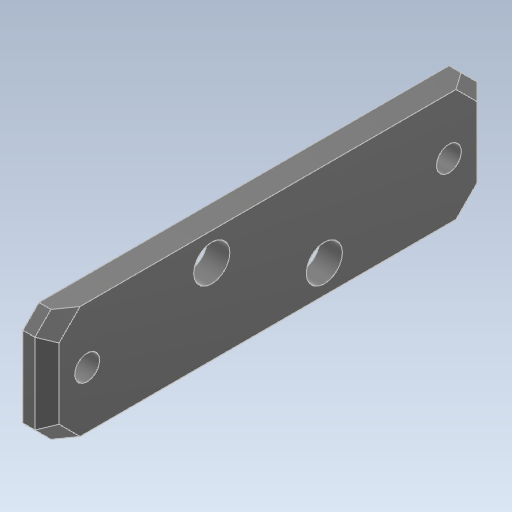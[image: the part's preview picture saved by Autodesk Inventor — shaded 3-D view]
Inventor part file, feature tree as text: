
AUTODESK INVENTOR PART (.ipt)
format: ipt  version: 2024 (Build 280153000, 153)  size: 151,040 bytes
history: native  units: mm
features: extrude x3, sketch x2, chamfer x2, other x1
ambient origin geometry x8: Origin, YZ Plane, XZ Plane, XY Plane, X Axis, Y Axis, Z Axis, Center Point
bodies: Body1 (feature_tree)
feature tree (8):
  other  "ソリッド1"
  sketch  "スケッチ1"
  sketch  "スケッチ2"
  extrude  "押し出し1"  Depth=45.0mm
  extrude  "押し出し2"  Depth=14.0mm
  extrude  "押し出し3"  Depth=55.0mm
  chamfer  "面取り1"  Distance=4.5mm
  chamfer  "面取り2"  Distance=3.1mm
